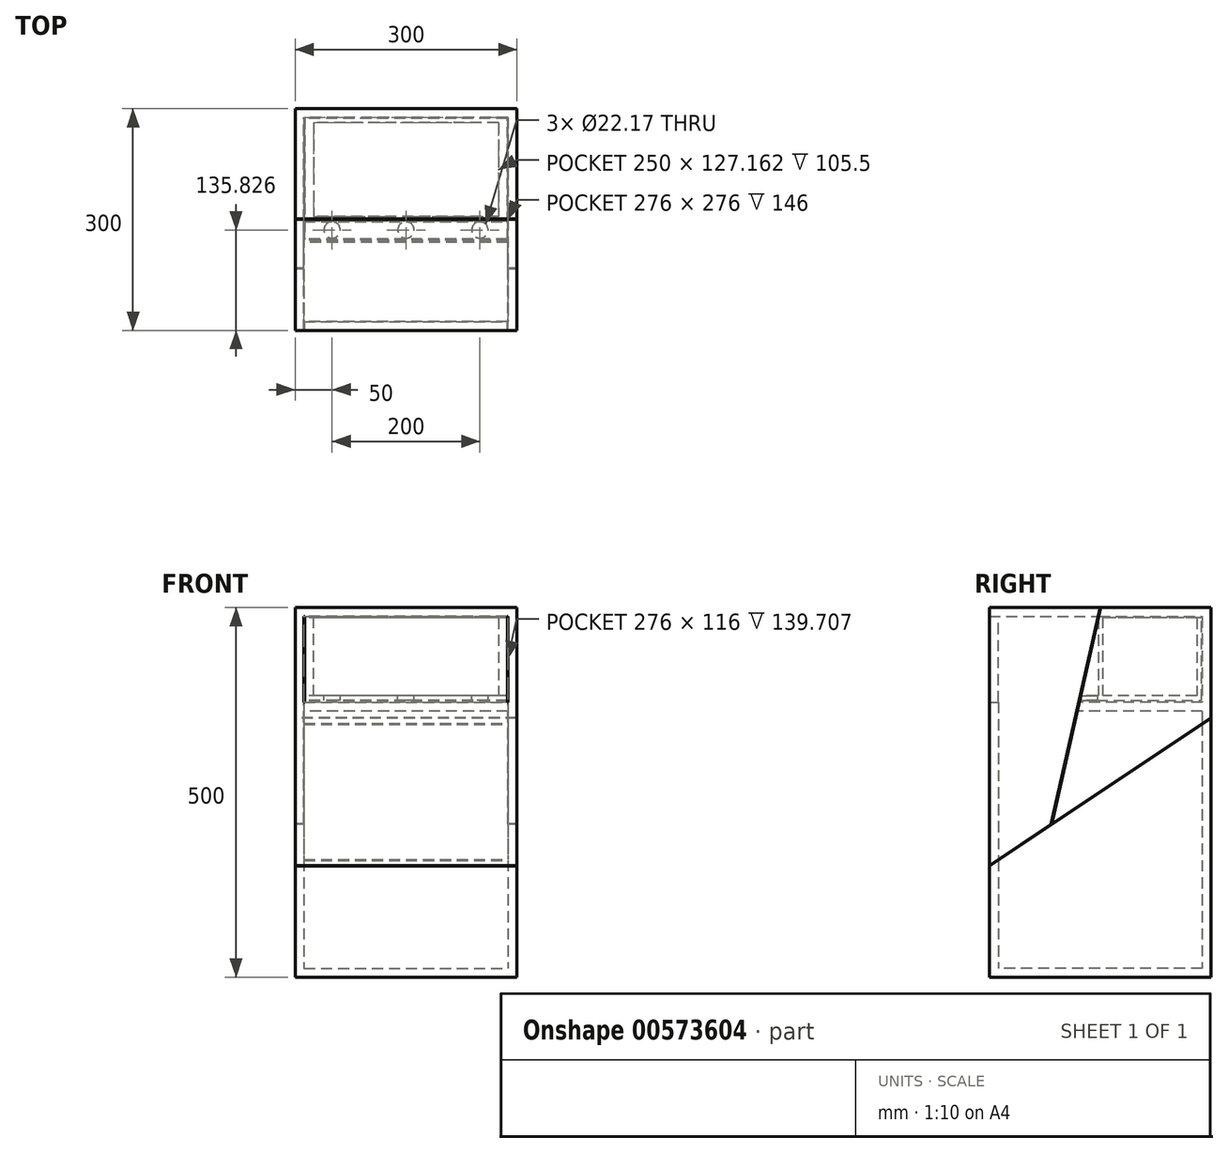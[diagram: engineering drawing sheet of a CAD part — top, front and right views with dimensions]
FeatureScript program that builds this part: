
annotation { "Feature Type Name" : "Feature", "Feature Type Description" : "" }
export const myFeature = defineFeature(function(context is Context, id is Id, definition is map)
    precondition{}
    {
        {
            var Q0;
            Q0=qCreatedBy(makeId("Top.planeOp"),FACE);
            var sketch = newSketch(context, id + "F0", { "sketchPlane" : qUnion([Q0])});
            skLineSegment(sketch, "E0.bottom", {"start": v(150, -150) * mm, "end": v(-150, -150) * mm});
            skLineSegment(sketch, "E0.top", {"start": v(150, 150) * mm, "end": v(-150, 150) * mm});
            skLineSegment(sketch, "E0.left", {"start": v(150, -150) * mm, "end": v(150, 150) * mm});
            skLineSegment(sketch, "E0.right", {"start": v(-150, -150) * mm, "end": v(-150, 150) * mm});
            skPoint(sketch, "E0.middle", {"position": v(0, 0) * mm});
            skLineSegment(sketch, "E1.bottom", {"start": v(138, -138) * mm, "end": v(-138, -138) * mm});
            skLineSegment(sketch, "E1.top", {"start": v(138, 138) * mm, "end": v(-138, 138) * mm});
            skLineSegment(sketch, "E1.left", {"start": v(138, -138) * mm, "end": v(138, 138) * mm});
            skLineSegment(sketch, "E1.right", {"start": v(-138, -138) * mm, "end": v(-138, 138) * mm});
            skSolve(sketch);
        }
        {
            var Q0;
            Q0 = qSketchRegion(id + "F0", true);
            var Q1;
            Q1=makeQuery(id+"F0.imprint","IMPRINT",FACE,{"disambiguationData":[TD([[makeQuery(id+"F0.imprint","IMPRINT",EDGE,{"derivedFrom":sQuery(id+"F0.wireOp",EDGE,"E1.bottom")}),-1.0]])]});
            extrude(context, id + "F1", {"entities" : qUnion([Q0, Q1]), "depth" : 12 * mm, "offsetDistance" : 25 * mm});
        }
        {
            var Q0;
            Q0=makeQuery(id+"F0.imprint","IMPRINT",FACE,{"disambiguationData":[TD([[makeQuery(id+"F0.imprint","IMPRINT",EDGE,{"derivedFrom":sQuery(id+"F0.wireOp",EDGE,"E0.bottom")}),-1.0]])]});
            extrude(context, id + "F2", {"entities" : qUnion([Q0]), "operationType" : NewBodyOperationType.ADD, "depth" : 500 * mm, "offsetDistance" : 25 * mm});
        }
        {
            var Q0;
            Q0=makeQuery(id+"F0.imprint","IMPRINT",FACE,{"disambiguationData":[TD([[makeQuery(id+"F0.imprint","IMPRINT",EDGE,{"derivedFrom":sQuery(id+"F0.wireOp",EDGE,"E1.bottom")}),-1.0]])]});
            var Q1;
            Q1=makeQuery(id+"F2.opExtrude","CAP_FACE",FACE,{"disambiguationData":[OSD([sQuery(id+"F0.wireOp",EDGE,"E0.bottom"),sQuery(id+"F0.wireOp",EDGE,"E0.top"),sQuery(id+"F0.wireOp",EDGE,"E0.left"),sQuery(id+"F0.wireOp",EDGE,"E0.right"),sQuery(id+"F0.wireOp",EDGE,"E1.bottom"),sQuery(id+"F0.wireOp",EDGE,"E1.top"),sQuery(id+"F0.wireOp",EDGE,"E1.left"),sQuery(id+"F0.wireOp",EDGE,"E1.right")])],"isStart":false});
            extrude(context, id + "F3", {"entities" : qUnion([Q0]), "operationType" : NewBodyOperationType.ADD, "endBound" : BoundingType.UP_TO_SURFACE, "depth" : 25 * mm, "endBoundEntityFace" : qUnion([Q1]), "offsetDistance" : 25 * mm, "hasSecondDirection" : true, "secondDirectionOppositeDirection" : false, "secondDirectionDepth" : (500 - (12)) * mm});
        }
        {
            var Q0;
            {var subQ0=sQuery(id+"F0.wireOp",EDGE,"E0.right");Q0=makeQuery(id+"F2.boolean.opBoolean","MERGE",FACE,{"derivedFrom":[makeQuery(id+"F1.opExtrude","SWEPT_FACE",FACE,{"disambiguationData":[OSD([subQ0])]}),makeQuery(id+"F2.opExtrude","SWEPT_FACE",FACE,{"disambiguationData":[OSD([subQ0])]})]});}
            var sketch = newSketch(context, id + "F4", { "sketchPlane" : qUnion([Q0])});
            skLineSegment(sketch, "E2", {"start": v(-150, 350) * mm, "end": v(150, 150) * mm});
            skLineSegment(sketch, "E3", {"start": v(-150, 351.2) * mm, "end": v(150, 151.2) * mm});
            skLineSegment(sketch, "E4", {"start": v(66.8, 206.67) * mm, "end": v(0, 500) * mm});
            skLineSegment(sketch, "E5", {"start": v(65.59, 207.48) * mm, "end": v(-1.03, 500) * mm});
            skLineSegment(sketch, "E6", {"start": v(-150, 360) * mm, "end": v(30.85, 360) * mm});
            skLineSegment(sketch, "E7", {"start": v(-150, 372) * mm, "end": v(28.12, 372) * mm});
            skLineSegment(sketch, "E8", {"start": v(27.55, 374.5) * mm, "end": v(-137, 374.5) * mm});
            skLineSegment(sketch, "E9", {"start": v(-137, 374.5) * mm, "end": v(-137, 486) * mm});
            skLineSegment(sketch, "E10", {"start": v(-137, 486) * mm, "end": v(2.16, 486) * mm});
            skLineSegment(sketch, "E11", {"start": v(-131, 486) * mm, "end": v(-131, 380.5) * mm});
            skLineSegment(sketch, "E12", {"start": v(-131, 380.5) * mm, "end": v(26.19, 380.5) * mm});
            skLineSegment(sketch, "E13", {"start": v(2.16, 486) * mm, "end": v(2.16, 374.5) * mm});
            skLineSegment(sketch, "E14", {"start": v(-3.84, 486) * mm, "end": v(-3.84, 374.5) * mm});
            skSolve(sketch);
        }
        {
            var Q0;
            {var subQ10=sQuery(id+"F4.wireOp",EDGE,"E2");Q0=makeQuery(id+"F4.imprint","IMPRINT",FACE,{"disambiguationData":[TD([[makeQuery(id+"F4.imprint","IMPRINT",EDGE,{"derivedFrom":subQ10}),1.0]])]});}
            var Q1;
            {var subQ5=sQuery(id+"F4.wireOp",EDGE,"E4");Q1=makeQuery(id+"F4.imprint","IMPRINT",FACE,{"disambiguationData":[TD([[makeQuery(id+"F4.imprint","IMPRINT",EDGE,{"derivedFrom":subQ5}),1.0]])]});}
            var Q2;
            {var subQ0=sQuery(id+"F0.wireOp",EDGE,"E0.left");Q2=makeQuery(id+"F2.boolean.opBoolean","MERGE",FACE,{"derivedFrom":[makeQuery(id+"F1.opExtrude","SWEPT_FACE",FACE,{"disambiguationData":[OSD([subQ0])]}),makeQuery(id+"F2.opExtrude","SWEPT_FACE",FACE,{"disambiguationData":[OSD([subQ0])]})]});}
            extrude(context, id + "F5", {"entities" : qUnion([Q0, Q1]), "operationType" : NewBodyOperationType.REMOVE, "endBound" : BoundingType.UP_TO_SURFACE, "oppositeDirection" : true, "depth" : 25 * mm, "endBoundEntityFace" : qUnion([Q2]), "offsetDistance" : 25 * mm});
        }
        {
            var Q0;
            {var subQ0=sQuery(id+"F4.wireOp",EDGE,"E6");Q0=makeQuery(id+"F4.imprint","IMPRINT",FACE,{"disambiguationData":[TD([[makeQuery(id+"F4.imprint","IMPRINT",EDGE,{"derivedFrom":subQ0}),1.0]])]});}
            var Q1;
            {var subQ6=sQuery(id+"F0.wireOp",EDGE,"E0.left");var subQ9=sQuery(id+"F4.wireOp",EDGE,"E5");Q1=makeQuery(id+"F5.boolean.opBoolean","SPLIT",FACE,{"disambiguationData":[TD([makeQuery(id+"F5.opExtrude","SWEPT_FACE",FACE,{"disambiguationData":[OSD([subQ9])]})])],"derivedFrom":makeQuery(id+"F2.boolean.opBoolean","MERGE",FACE,{"derivedFrom":[makeQuery(id+"F1.opExtrude","SWEPT_FACE",FACE,{"disambiguationData":[OSD([subQ6])]}),makeQuery(id+"F2.opExtrude","SWEPT_FACE",FACE,{"disambiguationData":[OSD([subQ6])]})]})});}
            extrude(context, id + "F6", {"entities" : qUnion([Q0]), "operationType" : NewBodyOperationType.ADD, "endBound" : BoundingType.UP_TO_SURFACE, "oppositeDirection" : true, "depth" : 25 * mm, "endBoundEntityFace" : qUnion([Q1]), "offsetDistance" : 25 * mm});
        }
        {
            var Q0;
            {var subQ1=sQuery(id+"F4.wireOp",EDGE,"E9");Q0=makeQuery(id+"F4.imprint","IMPRINT",FACE,{"disambiguationData":[TD([[makeQuery(id+"F4.imprint","IMPRINT",EDGE,{"derivedFrom":subQ1}),-1.0]])]});}
            var Q1;
            {var subQ0=sQuery(id+"F4.wireOp",EDGE,"E8");var subQ1=sQuery(id+"F4.wireOp",EDGE,"E5");var subQ2=makeQuery(id+"F4.imprint","INTERSECT",VERTEX,{"derivedFrom":[subQ1,subQ0]});Q1=makeQuery(id+"F4.imprint","IMPRINT",FACE,{"disambiguationData":[TD([[makeQuery(id+"F4.imprint","IMPRINT",EDGE,{"disambiguationData":[TD([[subQ2,-1.0]])],"derivedFrom":subQ1}),1.0]])]});}
            var Q2;
            {var subQ0=sQuery(id+"F4.wireOp",EDGE,"E13");var subQ1=sQuery(id+"F4.wireOp",EDGE,"E8");var subQ2=makeQuery(id+"F4.imprint","INTERSECT",VERTEX,{"derivedFrom":[subQ1,subQ0]});Q2=makeQuery(id+"F4.imprint","IMPRINT",FACE,{"disambiguationData":[TD([[makeQuery(id+"F4.imprint","IMPRINT",EDGE,{"disambiguationData":[TD([[subQ2,-1.0]])],"derivedFrom":subQ1}),-1.0]])]});}
            var Q3;
            {var subQ3=sQuery(id+"F4.wireOp",EDGE,"E14");var subQ5=sQuery(id+"F4.wireOp",EDGE,"E12");var subQ7=makeQuery(id+"F4.imprint","INTERSECT",VERTEX,{"derivedFrom":[subQ5,subQ3]});Q3=makeQuery(id+"F4.imprint","IMPRINT",FACE,{"disambiguationData":[TD([[makeQuery(id+"F4.imprint","IMPRINT",EDGE,{"disambiguationData":[TD([[subQ7,-1.0]])],"derivedFrom":subQ5}),1.0]])]});}
            var Q4;
            {var subQ0=sQuery(id+"F4.wireOp",EDGE,"E5");var subQ1=makeQuery(id+"F5.opExtrude","SWEPT_FACE",FACE,{"disambiguationData":[OSD([subQ0])]});var subQ2=sQuery(id+"F0.wireOp",EDGE,"E1.left");Q4=makeQuery(id+"F6.boolean.opBoolean","SPLIT",FACE,{"disambiguationData":[TD([makeQuery(id+"F6.opExtrude","SWEPT_FACE",FACE,{"disambiguationData":[OSD([sQuery(id+"F4.wireOp",EDGE,"E7")])]})])],"derivedFrom":makeQuery(id+"F5.boolean.opBoolean","SPLIT",FACE,{"disambiguationData":[TD([subQ1])],"derivedFrom":makeQuery(id+"F2.opExtrude","SWEPT_FACE",FACE,{"disambiguationData":[OSD([subQ2])]})})});}
            extrude(context, id + "F7", {"entities" : qUnion([Q0, Q1, Q2, Q3]), "operationType" : NewBodyOperationType.ADD, "endBound" : BoundingType.UP_TO_SURFACE, "oppositeDirection" : true, "depth" : 25 * mm, "endBoundEntityFace" : qUnion([Q4]), "offsetDistance" : 25 * mm});
        }
        {
            var Q0;
            {var subQ3=sQuery(id+"F0.wireOp",EDGE,"E1.top");var subQ6=sQuery(id+"F4.wireOp",EDGE,"E3");Q0=makeQuery(id+"F6.boolean.opBoolean","SPLIT",FACE,{"disambiguationData":[TD([makeQuery(id+"F6.opExtrude","SWEPT_FACE",FACE,{"disambiguationData":[OSD([sQuery(id+"F4.wireOp",EDGE,"E7")])]})])],"derivedFrom":makeQuery(id+"F5.boolean.opBoolean","SPLIT",FACE,{"disambiguationData":[TD([makeQuery(id+"F5.opExtrude","SWEPT_FACE",FACE,{"disambiguationData":[OSD([subQ6]),TDD([makeQuery(id+"F4.imprint","IMPRINT",EDGE,{"disambiguationData":[TD([[makeQuery(id+"F4.imprint","INTERSECT",VERTEX,{"derivedFrom":[subQ6,sQuery(id+"F4.wireOp",EDGE,"E5")]}),1.0]])],"derivedFrom":subQ6})])]})])],"derivedFrom":makeQuery(id+"F2.opExtrude","SWEPT_FACE",FACE,{"disambiguationData":[OSD([subQ3])]})})});}
            var sketch = newSketch(context, id + "F8", { "sketchPlane" : qUnion([Q0])});
            skLineSegment(sketch, "E15", {"start": v(-137, 488) * mm, "end": v(-137, 372) * mm});
            skLineSegment(sketch, "E16", {"start": v(137, 488) * mm, "end": v(137, 372) * mm});
            skSolve(sketch);
        }
        {
            var Q0;
            {var subQ0=sQuery(id+"F8.wireOp",EDGE,"E15");Q0=makeQuery(id+"F8.imprint","IMPRINT",FACE,{"disambiguationData":[TD([[makeQuery(id+"F8.imprint","IMPRINT",EDGE,{"derivedFrom":subQ0}),-1.0]])]});}
            var Q1;
            {var subQ0=sQuery(id+"F8.wireOp",EDGE,"E16");Q1=makeQuery(id+"F8.imprint","IMPRINT",FACE,{"disambiguationData":[TD([[makeQuery(id+"F8.imprint","IMPRINT",EDGE,{"derivedFrom":subQ0}),1.0]])]});}
            extrude(context, id + "F9", {"entities" : qUnion([Q0, Q1]), "operationType" : NewBodyOperationType.REMOVE, "depth" : 500 * mm, "offsetDistance" : 25 * mm});
        }
        {
            var Q0;
            Q0=makeQuery(id+"F7.opExtrude","SWEPT_FACE",FACE,{"disambiguationData":[OSD([sQuery(id+"F4.wireOp",EDGE,"E13")])]});
            var sketch = newSketch(context, id + "F10", { "sketchPlane" : qUnion([Q0])});
            skLineSegment(sketch, "E17", {"start": v(-125, 380.5) * mm, "end": v(-125, 486) * mm});
            skLineSegment(sketch, "E18", {"start": v(125, 486) * mm, "end": v(125, 380.5) * mm});
            skSolve(sketch);
        }
        {
            var Q0;
            {var subQ0=sQuery(id+"F10.wireOp",EDGE,"E17");Q0=makeQuery(id+"F10.imprint","IMPRINT",FACE,{"disambiguationData":[TD([[makeQuery(id+"F10.imprint","IMPRINT",EDGE,{"derivedFrom":subQ0}),1.0]])]});}
            var Q1;
            {var subQ0=sQuery(id+"F10.wireOp",EDGE,"E18");Q1=makeQuery(id+"F10.imprint","IMPRINT",FACE,{"disambiguationData":[TD([[makeQuery(id+"F10.imprint","IMPRINT",EDGE,{"derivedFrom":subQ0}),1.0]])]});}
            var Q2;
            Q2=makeQuery(id+"F7.opExtrude","SWEPT_FACE",FACE,{"disambiguationData":[OSD([sQuery(id+"F4.wireOp",EDGE,"E11")])]});
            extrude(context, id + "F11", {"entities" : qUnion([Q0, Q1]), "operationType" : NewBodyOperationType.ADD, "endBound" : BoundingType.UP_TO_SURFACE, "oppositeDirection" : true, "depth" : 25 * mm, "endBoundEntityFace" : qUnion([Q2]), "offsetDistance" : 25 * mm});
        }
        {
            var Q0;
            {var subQ0=sQuery(id+"F4.wireOp",EDGE,"E12");Q0=makeQuery(id+"F7.opExtrude","SWEPT_FACE",FACE,{"disambiguationData":[OSD([subQ0]),TDD([makeQuery(id+"F4.imprint","IMPRINT",EDGE,{"disambiguationData":[TD([[makeQuery(id+"F4.imprint","INTERSECT",VERTEX,{"derivedFrom":[sQuery(id+"F4.wireOp",EDGE,"E5"),subQ0]}),1.0]])],"derivedFrom":subQ0})])]});}
            var sketch = newSketch(context, id + "F12", { "sketchPlane" : qUnion([Q0])});
            skLineSegment(sketch, "E19", {"start": v(-137, -14.17) * mm, "end": v(137, -14.17) * mm, "construction": true});
            skCircle(sketch, "E20", {"center": v(-300, -14.17) * mm, "radius": 11.09 * mm});
            skCircle(sketch, "E21", {"center": v(-200, -14.17) * mm, "radius": 11.09 * mm});
            skCircle(sketch, "E22", {"center": v(-100, -14.17) * mm, "radius": 11.09 * mm});
            skCircle(sketch, "E23", {"center": v(0, -14.17) * mm, "radius": 11.09 * mm});
            skCircle(sketch, "E24", {"center": v(100, -14.17) * mm, "radius": 11.09 * mm});
            skSolve(sketch);
        }
        {
            var Q0;
            Q0=makeQuery(id+"F12.imprint","IMPRINT",FACE,{"disambiguationData":[TD([[makeQuery(id+"F12.imprint","IMPRINT",EDGE,{"derivedFrom":sQuery(id+"F12.wireOp",EDGE,"E20")}),1.0]])]});
            var Q1;
            Q1=makeQuery(id+"F12.imprint","IMPRINT",FACE,{"disambiguationData":[TD([[makeQuery(id+"F12.imprint","IMPRINT",EDGE,{"derivedFrom":sQuery(id+"F12.wireOp",EDGE,"E21")}),1.0]])]});
            var Q2;
            Q2=makeQuery(id+"F12.imprint","IMPRINT",FACE,{"disambiguationData":[TD([[makeQuery(id+"F12.imprint","IMPRINT",EDGE,{"derivedFrom":sQuery(id+"F12.wireOp",EDGE,"E22")}),1.0]])]});
            var Q3;
            Q3=makeQuery(id+"F12.imprint","IMPRINT",FACE,{"disambiguationData":[TD([[makeQuery(id+"F12.imprint","IMPRINT",EDGE,{"derivedFrom":sQuery(id+"F12.wireOp",EDGE,"E23")}),1.0]])]});
            var Q4;
            Q4=makeQuery(id+"F12.imprint","IMPRINT",FACE,{"disambiguationData":[TD([[makeQuery(id+"F12.imprint","IMPRINT",EDGE,{"derivedFrom":sQuery(id+"F12.wireOp",EDGE,"E24")}),1.0]])]});
            var Q5;
            Q5=makeQuery(id+"F7.opExtrude","SWEPT_FACE",FACE,{"disambiguationData":[OSD([sQuery(id+"F4.wireOp",EDGE,"E8")])]});
            extrude(context, id + "F13", {"entities" : qUnion([Q0, Q1, Q2, Q3, Q4]), "operationType" : NewBodyOperationType.REMOVE, "endBound" : BoundingType.UP_TO_SURFACE, "oppositeDirection" : true, "depth" : 25 * mm, "endBoundEntityFace" : qUnion([Q5]), "offsetDistance" : 25 * mm});
        }
    });
